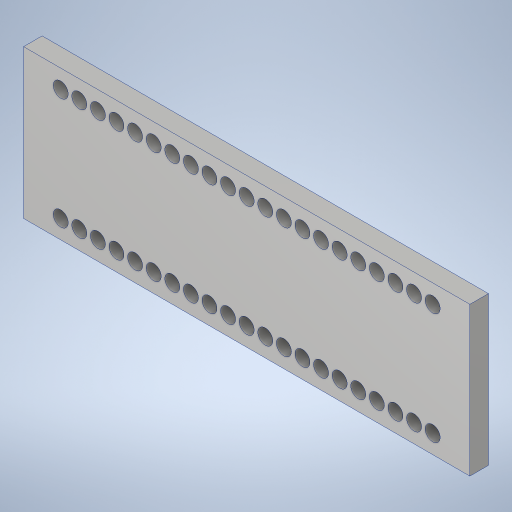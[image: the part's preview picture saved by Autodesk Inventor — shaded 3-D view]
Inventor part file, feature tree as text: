
AUTODESK INVENTOR PART (.ipt)
format: ipt  version: 2023.4 (Build 274418000, 418)  size: 301,056 bytes
history: native  units: in
note: dims shown in document units (in); Inventor stores cm internally (conversion verified against a paired STEP export)
features: sketch x2, extrude x1, hole x1
ambient origin geometry x8: Origin, YZ Plane, XZ Plane, XY Plane, X Axis, Y Axis, Z Axis, Center Point
bodies: Solid1 (feature_tree)
feature tree (4):
  extrude  "Extrusion1"  Depth=2.0in
  hole  "Hole1"  [1 undecoded]
  sketch  "Sketch1"  dims[d0=6.0in d1=2.0in]
  sketch  "Sketch2"  dims[d2=0.25in d3=0.0in d4=0.5in d5=0.25in d6=8.2677in d8=0.25in d9=0.3937in d11=1.0in d13=0.25in d14=0.201in d15=0.75in d16=0.385in d17=0.25in d18=0.5635in d19=1.0in d20=0.8108in]
note: 1 required parameter value undecoded (feature->parameter linkage not recoverable at this tier; creation-order binding heuristic only, values carry confidence <= 0.55)
